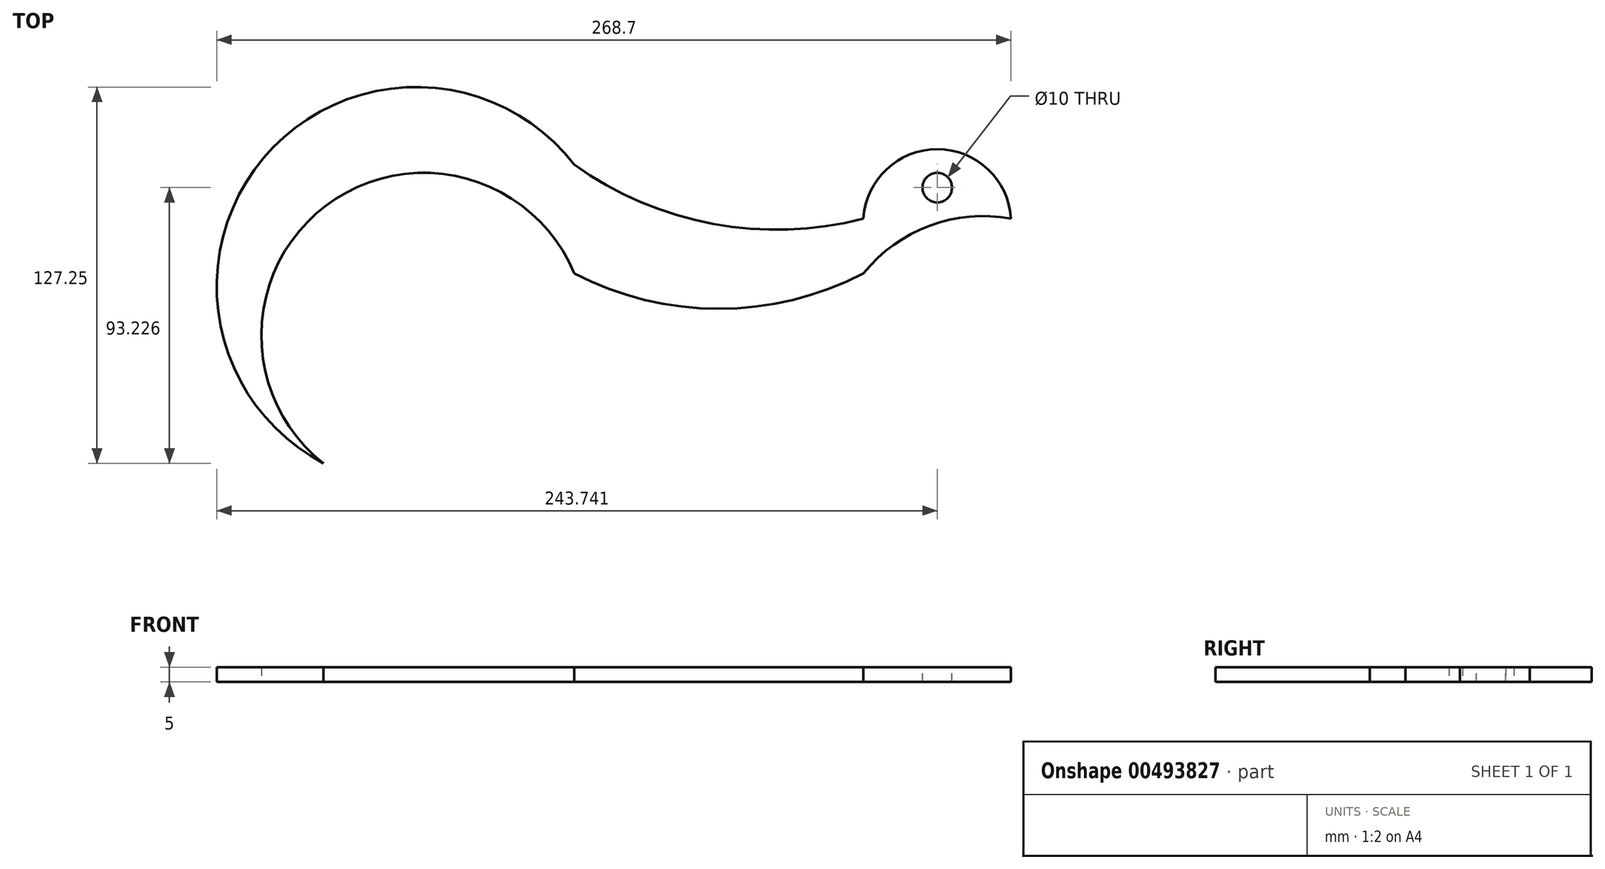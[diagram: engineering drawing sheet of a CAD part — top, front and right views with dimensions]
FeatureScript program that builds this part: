
annotation { "Feature Type Name" : "Feature", "Feature Type Description" : "" }
export const myFeature = defineFeature(function(context is Context, id is Id, definition is map)
    precondition{}
    {
        {
            var Q0;
            Q0=qCreatedBy(makeId("Top.planeOp"),FACE);
            var sketch = newSketch(context, id + "F0", { "sketchPlane" : qUnion([Q0])});
            skArc(sketch, "E0", {"start": v(84.84, 60.47) * mm, "mid": v(-20.27, 62.64) * mm, "end": v(0, -40.53) * mm});
            skArc(sketch, "E1", {"start": v(84.84, 60.47) * mm, "mid": v(131.74, 40.48) * mm, "end": v(182.7, 42.19) * mm});
            skArc(sketch, "E2", {"start": v(232.6, 42.19) * mm, "mid": v(207.65, 65.71) * mm, "end": v(182.7, 42.19) * mm});
            skArc(sketch, "E3", {"start": v(84.84, 23.7) * mm, "mid": v(0.82, 46.55) * mm, "end": v(0, -40.53) * mm});
            skArc(sketch, "E4", {"start": v(84.84, 23.7) * mm, "mid": v(133.77, 11.68) * mm, "end": v(182.7, 23.7) * mm});
            skArc(sketch, "E5", {"start": v(232.6, 42.19) * mm, "mid": v(205.1, 39.84) * mm, "end": v(182.7, 23.7) * mm});
            skSolve(sketch);
        }
        {
            var Q0;
            Q0=makeQuery(id+"F0.imprint","IMPRINT",FACE,{"disambiguationData":[TD([[makeQuery(id+"F0.imprint","IMPRINT",EDGE,{"derivedFrom":sQuery(id+"F0.wireOp",EDGE,"E0")}),1.0]])]});
            extrude(context, id + "F1", {"entities" : qUnion([Q0]), "depth" : 5 * mm});
        }
        {
            var Q0;
            Q0=qCreatedBy(makeId("Top.planeOp"),FACE);
            var sketch = newSketch(context, id + "F2", { "sketchPlane" : qUnion([Q0])});
            skCircle(sketch, "E6", {"center": v(210.54, 54.14) * mm, "radius": 5 * mm});
            skSolve(sketch);
        }
        {
            var Q0;
            Q0 = qSketchRegion(id + "F2", true);
            extrude(context, id + "F3", {"entities" : qUnion([Q0]), "operationType" : NewBodyOperationType.REMOVE, "endBound" : BoundingType.THROUGH_ALL, "oppositeDirection" : true, "depth" : 25 * mm});
        }
        {
            var Q0;
            Q0=makeQuery(id+"F1.opExtrude","CAP_FACE",FACE,{"disambiguationData":[OSD([sQuery(id+"F0.wireOp",EDGE,"E0"),sQuery(id+"F0.wireOp",EDGE,"E1"),sQuery(id+"F0.wireOp",EDGE,"E2"),sQuery(id+"F0.wireOp",EDGE,"E3"),sQuery(id+"F0.wireOp",EDGE,"E4"),sQuery(id+"F0.wireOp",EDGE,"E5")])],"isStart":false});
            var sketch = newSketch(context, id + "F4", { "sketchPlane" : qUnion([Q0])});
            skPoint(sketch, "E7", {"position": v(207.65, 52.7) * mm});
            skPoint(sketch, "E7.positionSnap0", {"position": v(207.65, 65.71) * mm});
            skCircle(sketch, "E8", {"center": v(207.65, 52.7) * mm, "radius": 5 * mm});
            skSolve(sketch);
        }
        {
            var Q0;
            Q0 = qSketchRegion(id + "F4", true);
            extrude(context, id + "F5", {"entities" : qUnion([Q0]), "operationType" : NewBodyOperationType.REMOVE, "endBound" : BoundingType.THROUGH_ALL, "oppositeDirection" : true, "depth" : 25 * mm});
        }
    });
